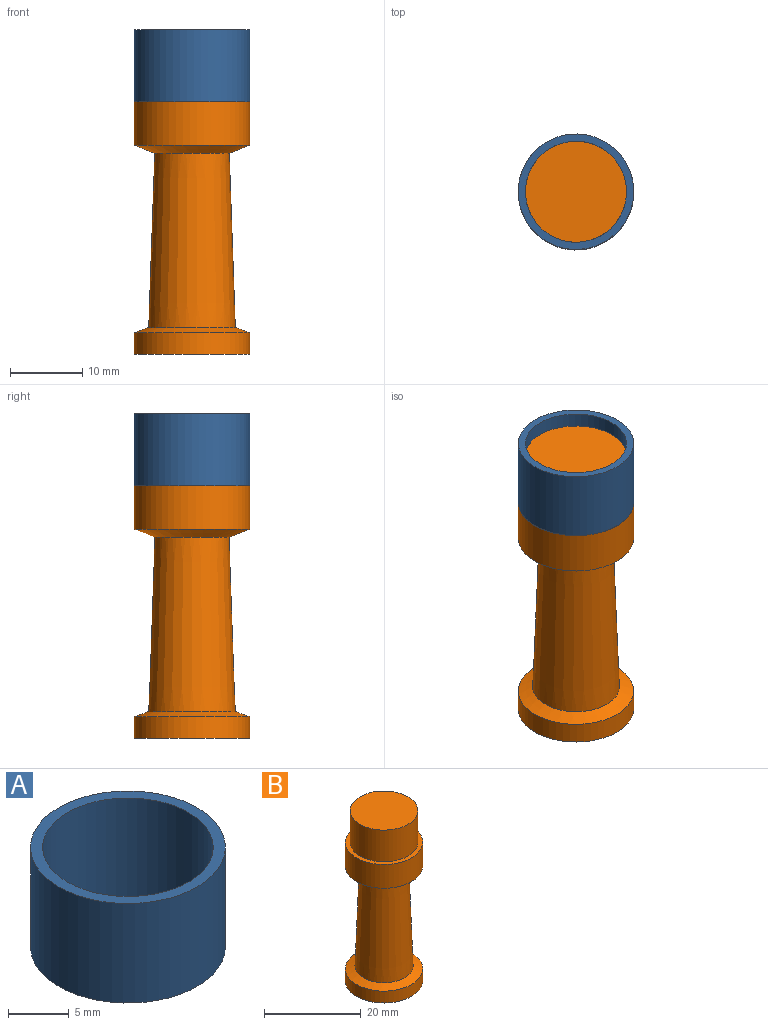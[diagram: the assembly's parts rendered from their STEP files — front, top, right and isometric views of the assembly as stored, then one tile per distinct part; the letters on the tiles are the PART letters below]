
ASSEMBLY  parts=2 mates=1
PART A: 4 faces, bbox 16x16x10 mm
  f0: cylinder r=7mm len=14mm, axis (0,0,-1), area 439.8mm2, adj f1,f3
  f1: plane 16x16mm, normal (0,0,-1), area 47.1mm2, adj f0,f2
  f2: cylinder r=8mm len=16mm, axis (0,0,-1), area 502.7mm2, adj f1,f3
  f3: plane 16x16mm, normal (0,0,1), area 47.1mm2, adj f0,f2
PART B: 9 faces, bbox 16x16x43 mm
  f0: plane 16x16mm, normal (0,0,-1), area 201.1mm2, adj f1
  f1: cylinder r=8mm len=16mm, axis (0,0,1), area 150.8mm2, adj f0,f2
  f2: cone r=8mm half-angle=70deg, axis (0,0,-1), area 93.6mm2, adj f1,f3
  f3: cone r=6mm half-angle=2deg, axis (0,0,-1), area 846.1mm2, adj f2,f4
  f4: cone r=5.16mm half-angle=68deg, axis (0,0,1), area 126.7mm2, adj f3,f5
  f5: cylinder r=8mm len=16mm, axis (0,0,1), area 301.6mm2, adj f4,f6
  f6: plane 16x16mm, normal (0,0,1), area 47.1mm2, adj f5,f7
  f7: cylinder r=7mm len=14mm, axis (0,0,1), area 351.9mm2, adj f6,f8
  f8: plane 14x14mm, normal (0,0,1), area 153.9mm2, adj f7
PLACE A t=(0,0,35)mm
PLACE B at identity
MATE fastened A.f0 <-> B.f1  axis (0,0,-1) through (0,0,35)mm
